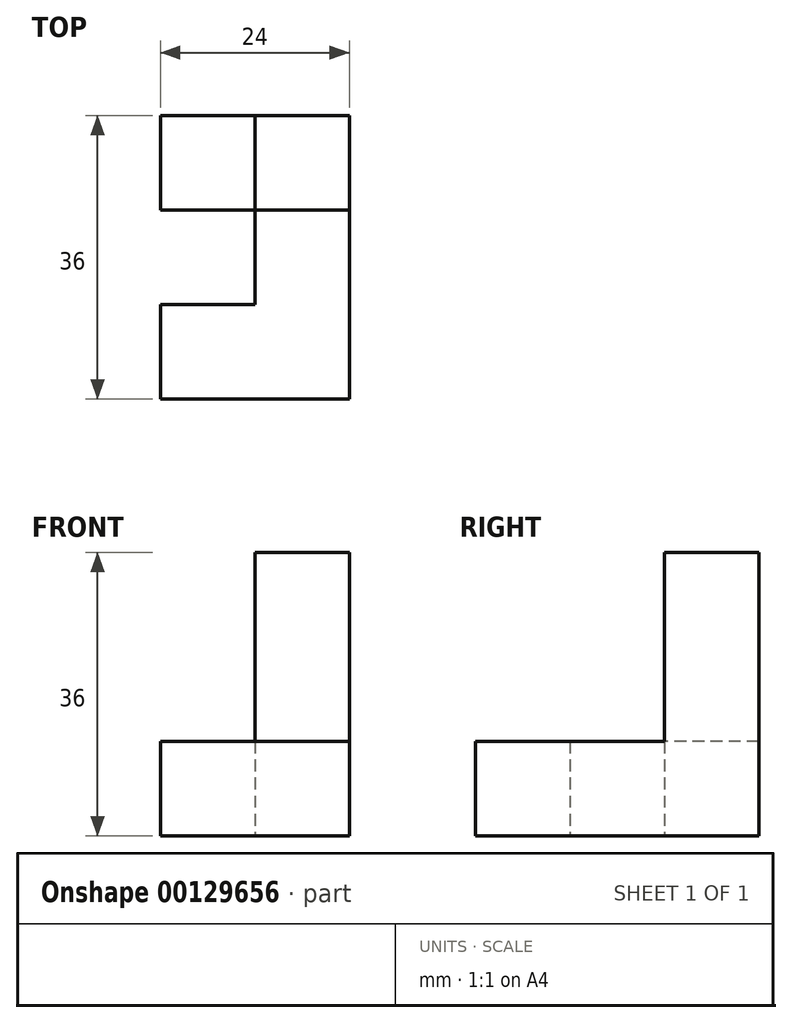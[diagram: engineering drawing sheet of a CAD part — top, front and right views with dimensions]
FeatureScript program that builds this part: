
annotation { "Feature Type Name" : "Feature", "Feature Type Description" : "" }
export const myFeature = defineFeature(function(context is Context, id is Id, definition is map)
    precondition{}
    {
        {
            var Q0;
            Q0=qCreatedBy(makeId("Top.planeOp"),FACE);
            var sketch = newSketch(context, id + "F0", { "sketchPlane" : qUnion([Q0])});
            skLineSegment(sketch, "E0.bottom", {"start": v(-36.11, 36) * mm, "end": v(-24.11, 36) * mm});
            skLineSegment(sketch, "E0.top", {"start": v(-36.11, 24) * mm, "end": v(-24.11, 24) * mm});
            skLineSegment(sketch, "E0.left", {"start": v(-36.11, 36) * mm, "end": v(-36.11, 24) * mm});
            skLineSegment(sketch, "E0.right", {"start": v(-24.11, 36) * mm, "end": v(-24.11, 24) * mm});
            skLineSegment(sketch, "E1.top", {"start": v(-36.11, 12) * mm, "end": v(-24.11, 12) * mm});
            skLineSegment(sketch, "E1.left", {"start": v(-36.11, 24) * mm, "end": v(-36.11, 12) * mm});
            skLineSegment(sketch, "E1.right", {"start": v(-24.11, 24) * mm, "end": v(-24.11, 12) * mm});
            skLineSegment(sketch, "E2.bottom", {"start": v(-36.11, 24) * mm, "end": v(-48.11, 24) * mm});
            skLineSegment(sketch, "E2.top", {"start": v(-36.11, 36) * mm, "end": v(-48.11, 36) * mm});
            skLineSegment(sketch, "E2.left", {"start": v(-36.11, 24) * mm, "end": v(-36.11, 36) * mm});
            skLineSegment(sketch, "E2.right", {"start": v(-48.11, 24) * mm, "end": v(-48.11, 36) * mm});
            skLineSegment(sketch, "E3.top", {"start": v(-36.11, 0) * mm, "end": v(-24.11, 0) * mm});
            skLineSegment(sketch, "E3.left", {"start": v(-36.11, 12) * mm, "end": v(-36.11, 0) * mm});
            skLineSegment(sketch, "E3.right", {"start": v(-24.11, 12) * mm, "end": v(-24.11, 0) * mm});
            skLineSegment(sketch, "E4.bottom", {"start": v(-36.11, 0) * mm, "end": v(-48.11, 0) * mm});
            skLineSegment(sketch, "E4.top", {"start": v(-36.11, 12) * mm, "end": v(-48.11, 12) * mm});
            skLineSegment(sketch, "E4.left", {"start": v(-36.11, 0) * mm, "end": v(-36.11, 12) * mm});
            skLineSegment(sketch, "E4.right", {"start": v(-48.11, 0) * mm, "end": v(-48.11, 12) * mm});
            skSolve(sketch);
        }
        {
            var Q0;
            Q0=makeQuery(id+"F0.imprint","IMPRINT",FACE,{"disambiguationData":[TD([[makeQuery(id+"F0.imprint","IMPRINT",EDGE,{"derivedFrom":sQuery(id+"F0.wireOp",EDGE,"E0.bottom")}),-1.0]])]});
            extrude(context, id + "F1", {"entities" : qUnion([Q0]), "depth" : 36 * mm});
        }
        {
            var Q0;
            Q0 = qSketchRegion(id + "F0", true);
            extrude(context, id + "F2", {"entities" : qUnion([Q0]), "operationType" : NewBodyOperationType.ADD, "depth" : 12 * mm});
        }
    });
